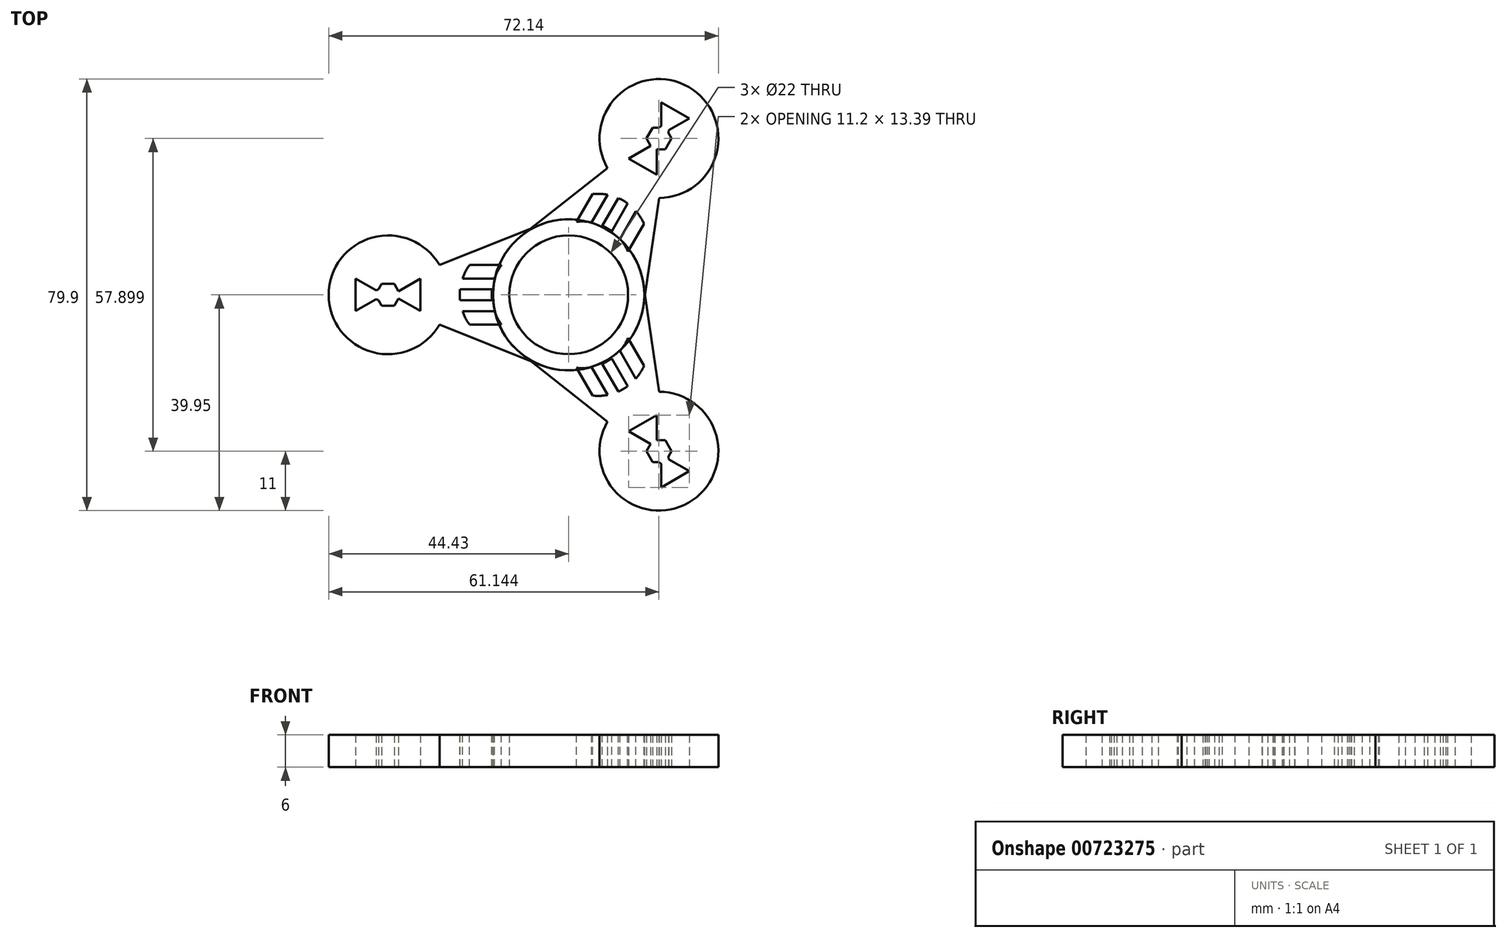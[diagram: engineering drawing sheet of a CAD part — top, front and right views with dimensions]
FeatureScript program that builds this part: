
annotation { "Feature Type Name" : "Feature", "Feature Type Description" : "" }
export const myFeature = defineFeature(function(context is Context, id is Id, definition is map)
    precondition{}
    {
        {
            var Q0;
            Q0=qCreatedBy(makeId("Top.planeOp"),FACE);
            var sketch = newSketch(context, id + "F0", { "sketchPlane" : qUnion([Q0])});
            skCircle(sketch, "E0", {"center": v(0, 0) * mm, "radius": 11 * mm});
            skCircle(sketch, "E1", {"center": v(0, 0) * mm, "radius": 14 * mm});
            skLineSegment(sketch, "E2", {"start": v(-5.2, 13) * mm, "end": v(-37.7, 0) * mm});
            skLineSegment(sketch, "E3", {"start": v(-37.7, 0) * mm, "end": v(-5.2, -13) * mm});
            skCircle(sketch, "E4", {"center": v(-33.43, 0) * mm, "radius": 11 * mm});
            skCircle(sketch, "E5.cCircle", {"center": v(-37.7, 0) * mm, "radius": 1.73 * mm, "construction": true});
            skLineSegment(sketch, "E5.0", {"start": v(-39.43, -3) * mm, "end": v(-39.43, 3) * mm});
            skLineSegment(sketch, "E5.1", {"start": v(-39.43, 3) * mm, "end": v(-35.34, 0.64) * mm});
            skLineSegment(sketch, "E5.2", {"start": v(-35.34, -0.64) * mm, "end": v(-39.43, -3) * mm});
            skPoint(sketch, "E5.0.midPoint", {"position": v(-39.43, 0) * mm});
            skCircle(sketch, "E6.cCircle", {"center": v(-29.16, 0) * mm, "radius": 1.73 * mm, "construction": true});
            skLineSegment(sketch, "E6.0", {"start": v(-27.43, 3) * mm, "end": v(-27.43, -3) * mm});
            skLineSegment(sketch, "E6.1", {"start": v(-27.43, -3) * mm, "end": v(-31.52, -0.64) * mm});
            skLineSegment(sketch, "E6.2", {"start": v(-31.52, 0.64) * mm, "end": v(-27.43, 3) * mm});
            skArc(sketch, "E7.cCircle", {"start": v(-31.52, 0.64) * mm, "mid": v(-33.43, 2.02) * mm, "end": v(-35.34, 0.64) * mm, "construction": true});
            skLineSegment(sketch, "E7.0", {"start": v(-35.17, 1) * mm, "end": v(-34.6, 2.02) * mm});
            skLineSegment(sketch, "E7.1", {"start": v(-34.6, 2.02) * mm, "end": v(-32.26, 2.02) * mm});
            skLineSegment(sketch, "E7.2", {"start": v(-32.26, 2.02) * mm, "end": v(-31.48, 0.66) * mm});
            skLineSegment(sketch, "E7.3", {"start": v(-31.48, -0.66) * mm, "end": v(-32.26, -2.02) * mm});
            skLineSegment(sketch, "E7.4", {"start": v(-32.26, -2.02) * mm, "end": v(-34.6, -2.02) * mm});
            skLineSegment(sketch, "E7.5", {"start": v(-34.6, -2.02) * mm, "end": v(-35.38, -0.66) * mm});
            skPoint(sketch, "E7.0.midPoint", {"position": v(-35.17, 1) * mm});
            skPoint(sketch, "E8.orphan", {"position": v(-31.1, 0) * mm});
            skPoint(sketch, "E9.orphan", {"position": v(-35.76, 0) * mm});
            skArc(sketch, "E10.trimOffspring", {"start": v(-35.34, -0.64) * mm, "mid": v(-33.43, -2.02) * mm, "end": v(-31.52, -0.64) * mm, "construction": true});
            skPoint(sketch, "E11.orphan", {"position": v(-34.23, 0) * mm});
            skPoint(sketch, "E12.orphan", {"position": v(-32.62, 0) * mm});
            skLineSegment(sketch, "E13", {"start": v(-35.8, 2.02) * mm, "end": v(-27.43, 2.02) * mm, "construction": true});
            skSolve(sketch);
        }
        {
            var Q0;
            Q0=qSketchRegion(id+"F0",true);
            extrude(context, id + "F1", {"entities" : qUnion([Q0]), "depth" : 6 * mm, "offsetDistance" : 25 * mm});
        }
        {
            var Q0;
            Q0=makeQuery(id+"F1.opExtrude","CAP_FACE",FACE,{"disambiguationData":[OSD([sQuery(id+"F0.wireOp",EDGE,"E0"),sQuery(id+"F0.wireOp",EDGE,"E1"),sQuery(id+"F0.wireOp",EDGE,"E2"),sQuery(id+"F0.wireOp",EDGE,"E3"),sQuery(id+"F0.wireOp",EDGE,"E4"),sQuery(id+"F0.wireOp",EDGE,"E5.0"),sQuery(id+"F0.wireOp",EDGE,"E5.1"),sQuery(id+"F0.wireOp",EDGE,"E5.2"),sQuery(id+"F0.wireOp",EDGE,"E6.0"),sQuery(id+"F0.wireOp",EDGE,"E6.1"),sQuery(id+"F0.wireOp",EDGE,"E6.2"),sQuery(id+"F0.wireOp",EDGE,"E7.0"),sQuery(id+"F0.wireOp",EDGE,"E7.1"),sQuery(id+"F0.wireOp",EDGE,"E7.2"),sQuery(id+"F0.wireOp",EDGE,"E7.3"),sQuery(id+"F0.wireOp",EDGE,"E7.4"),sQuery(id+"F0.wireOp",EDGE,"E7.5")])],"isStart":false});
            var sketch = newSketch(context, id + "F2", { "sketchPlane" : qUnion([Q0])});
            skLineSegment(sketch, "E14.bottom", {"start": v(-18.36, 5.51) * mm, "end": v(-13.84, 5.51) * mm});
            skLineSegment(sketch, "E14.top", {"start": v(-18.36, -5.51) * mm, "end": v(-13.84, -5.51) * mm});
            skArc(sketch, "E15", {"start": v(-12.43, 5.51) * mm, "mid": v(-14.24, 0) * mm, "end": v(-12.43, -5.51) * mm});
            skLineSegment(sketch, "E16", {"start": v(-13.84, 5.51) * mm, "end": v(-12.43, 5.51) * mm});
            skLineSegment(sketch, "E17", {"start": v(-13.84, -5.51) * mm, "end": v(-12.43, -5.51) * mm});
            skArc(sketch, "E18", {"start": v(-18.36, 5.51) * mm, "mid": v(-20.16, 0) * mm, "end": v(-18.36, -5.51) * mm});
            skSolve(sketch);
        }
        {
            var Q0;
            Q0=makeQuery(id+"F2.imprint","IMPRINT",FACE,{"disambiguationData":[TD([[makeQuery(id+"F2.imprint","IMPRINT",EDGE,{"derivedFrom":sQuery(id+"F2.wireOp",EDGE,"E14.bottom")}),-1.0]])]});
            var Q1;
            Q1=makeQuery(id+"F2.imprint","IMPRINT",FACE,{"disambiguationData":[TD([[makeQuery(id+"F2.imprint","IMPRINT",EDGE,{"derivedFrom":sQuery(id+"F2.wireOp",EDGE,"3aba4da8-8bb8-4d6b-b9dc-3ec0c25ae3a90.MirrorCS")}),-1.0]])]});
            extrude(context, id + "F3", {"entities" : qUnion([Q0, Q1]), "operationType" : NewBodyOperationType.REMOVE, "oppositeDirection" : true, "depth" : 25 * mm, "offsetDistance" : 25 * mm});
        }
        {
            var Q0;
            Q0=makeQuery(id+"F1.opExtrude","CAP_FACE",FACE,{"disambiguationData":[OSD([sQuery(id+"F0.wireOp",EDGE,"E0"),sQuery(id+"F0.wireOp",EDGE,"E1"),sQuery(id+"F0.wireOp",EDGE,"E2"),sQuery(id+"F0.wireOp",EDGE,"E3"),sQuery(id+"F0.wireOp",EDGE,"E4"),sQuery(id+"F0.wireOp",EDGE,"E5.0"),sQuery(id+"F0.wireOp",EDGE,"E5.1"),sQuery(id+"F0.wireOp",EDGE,"E5.2"),sQuery(id+"F0.wireOp",EDGE,"E6.0"),sQuery(id+"F0.wireOp",EDGE,"E6.1"),sQuery(id+"F0.wireOp",EDGE,"E6.2"),sQuery(id+"F0.wireOp",EDGE,"E7.0"),sQuery(id+"F0.wireOp",EDGE,"E7.1"),sQuery(id+"F0.wireOp",EDGE,"E7.2"),sQuery(id+"F0.wireOp",EDGE,"E7.3"),sQuery(id+"F0.wireOp",EDGE,"E7.4"),sQuery(id+"F0.wireOp",EDGE,"E7.5")])],"isStart":false});
            var sketch = newSketch(context, id + "F4", { "sketchPlane" : qUnion([Q0])});
            skLineSegment(sketch, "E19.bottom", {"start": v(-20.4, -3.01) * mm, "end": v(-13.32, -3.01) * mm});
            skLineSegment(sketch, "E19.top", {"start": v(-20.4, -1.01) * mm, "end": v(-13.32, -1.01) * mm});
            skLineSegment(sketch, "E19.left", {"start": v(-20.4, -3.01) * mm, "end": v(-20.4, -1.01) * mm});
            skLineSegment(sketch, "E19.right", {"start": v(-13.32, -3.01) * mm, "end": v(-13.32, -1.01) * mm});
            skLineSegment(sketch, "E20.bottom", {"start": v(-20.23, 3.01) * mm, "end": v(-11.96, 3.01) * mm});
            skLineSegment(sketch, "E20.top", {"start": v(-20.23, 1.01) * mm, "end": v(-11.96, 1.01) * mm});
            skLineSegment(sketch, "E20.left", {"start": v(-20.23, 3.01) * mm, "end": v(-20.23, 1.01) * mm});
            skLineSegment(sketch, "E20.right", {"start": v(-11.96, 3.01) * mm, "end": v(-11.96, 1.01) * mm});
            skSolve(sketch);
        }
        {
            var Q0;
            Q0=qSketchRegion(id+"F4",true);
            extrude(context, id + "F5", {"entities" : qUnion([Q0]), "operationType" : NewBodyOperationType.ADD, "oppositeDirection" : true, "depth" : 6 * mm, "offsetDistance" : 25 * mm});
        }
        {
            var Q0;
            Q0=makeQuery(id+"F1.opExtrude","SWEPT_BODY",BODY,{"disambiguationData":[OSD([sQuery(id+"F0.wireOp",EDGE,"E0"),sQuery(id+"F0.wireOp",EDGE,"E1"),sQuery(id+"F0.wireOp",EDGE,"E2"),sQuery(id+"F0.wireOp",EDGE,"E3"),sQuery(id+"F0.wireOp",EDGE,"E4"),sQuery(id+"F0.wireOp",EDGE,"E5.0"),sQuery(id+"F0.wireOp",EDGE,"E5.1"),sQuery(id+"F0.wireOp",EDGE,"E5.2"),sQuery(id+"F0.wireOp",EDGE,"E6.0"),sQuery(id+"F0.wireOp",EDGE,"E6.1"),sQuery(id+"F0.wireOp",EDGE,"E6.2"),sQuery(id+"F0.wireOp",EDGE,"E7.0"),sQuery(id+"F0.wireOp",EDGE,"E7.1"),sQuery(id+"F0.wireOp",EDGE,"E7.2"),sQuery(id+"F0.wireOp",EDGE,"E7.3"),sQuery(id+"F0.wireOp",EDGE,"E7.4"),sQuery(id+"F0.wireOp",EDGE,"E7.5")])]});
            var Q1;
            Q1=makeQuery(id+"F1.opExtrude","CAP_EDGE",EDGE,{"disambiguationData":[OSD([sQuery(id+"F0.wireOp",EDGE,"E0")])],"isStart":false});
            circularPattern(context, id + "F6", {"entities" : qUnion([Q0]), "axis" : qUnion([Q1]), "angle" : 360 * degree, "instanceCount" : 3, "equalSpace" : true});
        }
    });
